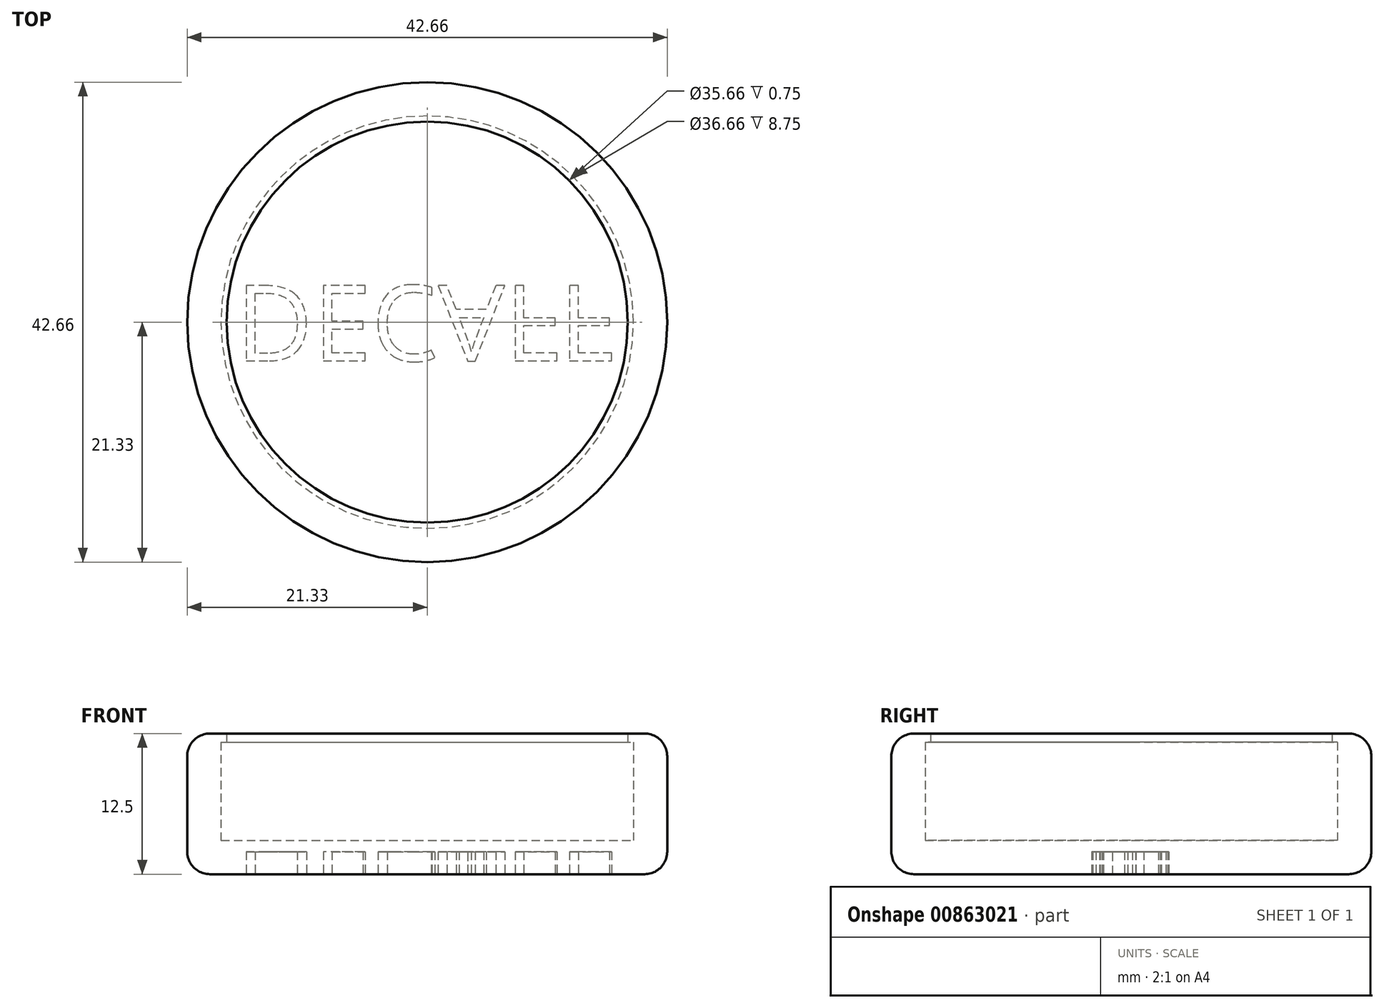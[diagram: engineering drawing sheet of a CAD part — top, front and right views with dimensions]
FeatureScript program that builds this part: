
annotation { "Feature Type Name" : "Feature", "Feature Type Description" : "" }
export const myFeature = defineFeature(function(context is Context, id is Id, definition is map)
    precondition{}
    {
        {
            var Q0;
            Q0=qCreatedBy(makeId("Front.planeOp"),FACE);
            var sketch = newSketch(context, id + "F0", { "sketchPlane" : qUnion([Q0])});
            skLineSegment(sketch, "E0", {"start": v(0, 0) * mm, "end": v(18.33, 0) * mm});
            skLineSegment(sketch, "E1", {"start": v(18.33, 0) * mm, "end": v(18.33, 8.75) * mm});
            skLineSegment(sketch, "E2", {"start": v(18.33, 8.75) * mm, "end": v(17.83, 8.75) * mm});
            skLineSegment(sketch, "E3", {"start": v(17.83, 8.75) * mm, "end": v(17.83, 9.5) * mm});
            skLineSegment(sketch, "E4", {"start": v(17.83, 9.5) * mm, "end": v(21.33, 9.5) * mm});
            skLineSegment(sketch, "E5", {"start": v(21.33, 9.5) * mm, "end": v(21.33, -3) * mm});
            skLineSegment(sketch, "E6", {"start": v(21.33, -3) * mm, "end": v(0, -3) * mm});
            skLineSegment(sketch, "E7", {"start": v(0, -3) * mm, "end": v(0, 0) * mm});
            skSolve(sketch);
        }
        {
            var Q0;
            Q0=makeQuery(id+"F0.imprint","IMPRINT",FACE,{"disambiguationData":[TD([[makeQuery(id+"F0.imprint","IMPRINT",EDGE,{"derivedFrom":sQuery(id+"F0.wireOp",EDGE,"E0")}),-1.0]])]});
            var Q1;
            Q1=sQuery(id+"F0.wireOp",EDGE,"E7");
            revolve(context, id + "F1", {"surfaceOperationType" : NewSurfaceOperationType.NEW, "entities" : qUnion([Q0]), "axis" : qUnion([Q1]), "revolveType" : RevolveType.FULL});
        }
        {
            var Q0;
            Q0=makeQuery(id+"F1.opRevolve","SWEPT_FACE",FACE,{"disambiguationData":[OSD([sQuery(id+"F0.wireOp",EDGE,"E6")])]});
            var sketch = newSketch(context, id + "F2", { "sketchPlane" : qUnion([Q0])});
            skText(sketch, "E8", { "text": "DECAFF", "fontName": "OpenSans-Regular.ttf"});
            const initialGuessF2  = {"E8": [-0.017, -0.00325, 1, 0, 0.00675]};
            skSetInitialGuess(sketch, initialGuessF2);
            skSolve(sketch);
        }
        {
            var Q0;
            Q0 = qSketchRegion(id + "F2", true);
            extrude(context, id + "F3", {"entities" : qUnion([Q0]), "operationType" : NewBodyOperationType.REMOVE, "oppositeDirection" : true, "depth" : 2 * mm, "offsetDistance" : 25 * mm});
        }
        {
            var Q0;
            Q0=makeQuery(id+"F1.opRevolve","SWEPT_EDGE",EDGE,{"disambiguationData":[OSD([sQuery(id+"F0.wireOp",EDGE,"E5"),sQuery(id+"F0.wireOp",EDGE,"E6")])]});
            var Q1;
            Q1=makeQuery(id+"F1.opRevolve","SWEPT_EDGE",EDGE,{"disambiguationData":[OSD([sQuery(id+"F0.wireOp",EDGE,"E4"),sQuery(id+"F0.wireOp",EDGE,"E5")])]});
            fillet(context, id + "F4", {"entities" : qUnion([Q0, Q1]), "radius" : 2 * mm, "tangentPropagation" : true, "allowEdgeOverflow" : false});
        }
    });
